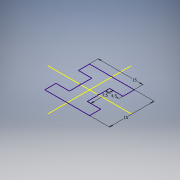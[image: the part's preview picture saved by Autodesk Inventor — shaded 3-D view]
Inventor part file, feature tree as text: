
AUTODESK INVENTOR PART (.ipt)
format: ipt  version: 2016 (Build 200138000, 138)  size: 87,040 bytes
history: native  units: mm
features: sketch x1
ambient origin geometry x8: Origin, YZ Plane, XZ Plane, XY Plane, X Axis, Y Axis, Z Axis, Center Point
feature tree (1):
  sketch  "Sketch1"  dims[d0=15.0mm d1=4.5mm d2=15.0mm d3=7.5mm]
